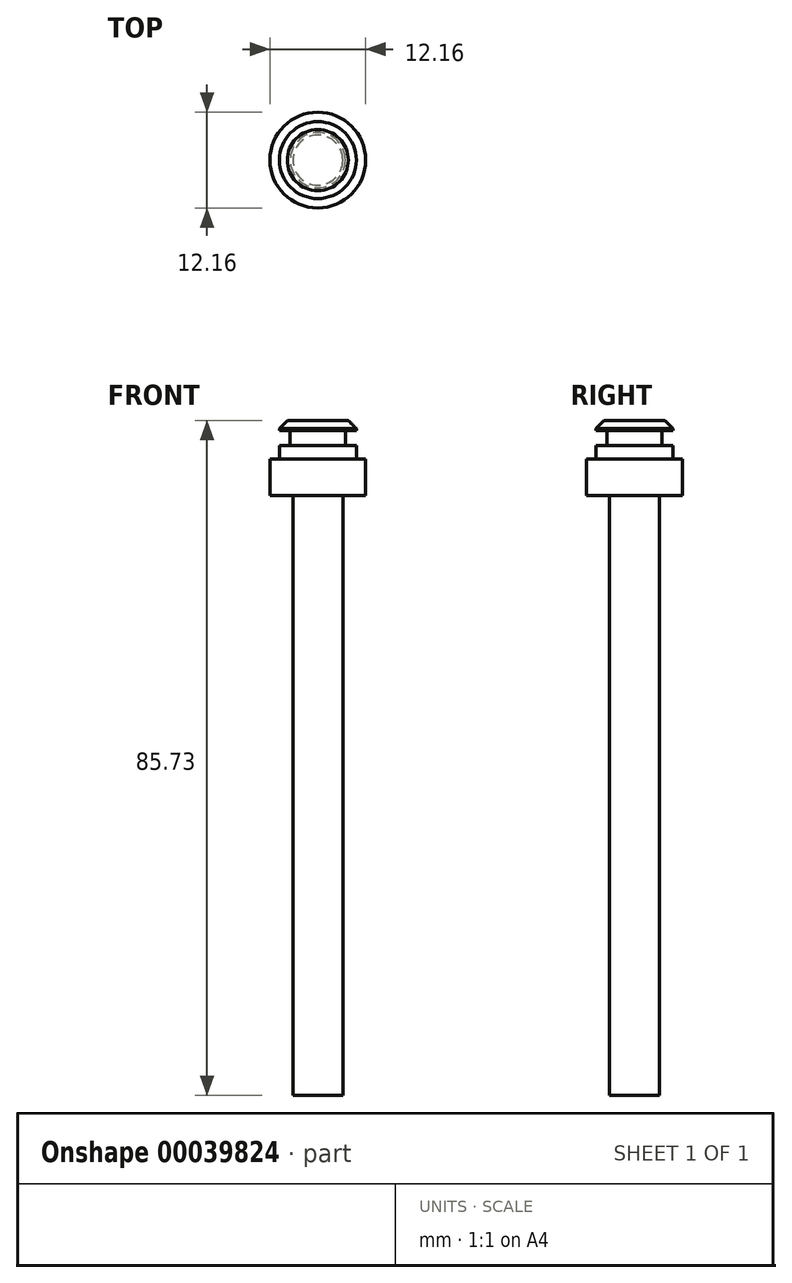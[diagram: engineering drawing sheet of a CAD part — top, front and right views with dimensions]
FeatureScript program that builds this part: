
annotation { "Feature Type Name" : "Feature", "Feature Type Description" : "" }
export const myFeature = defineFeature(function(context is Context, id is Id, definition is map)
    precondition{}
    {
        {
            var Q0;
            Q0=qCreatedBy(makeId("Top.planeOp"),FACE);
            var sketch = newSketch(context, id + "F0", { "sketchPlane" : qUnion([Q0])});
            skCircle(sketch, "E0", {"center": v(0, 0) * mm, "radius": 3.18 * mm});
            skSolve(sketch);
        }
        {
            var Q0;
            Q0 = qSketchRegion(id + "F0", true);
            extrude(context, id + "F1", {"entities" : qUnion([Q0]), "depth" : 76.2 * mm});
        }
        {
            var Q0;
            Q0=makeQuery(id+"F1.opExtrude","CAP_FACE",FACE,{"disambiguationData":[OSD([sQuery(id+"F0.wireOp",EDGE,"E0")])],"isStart":false});
            var sketch = newSketch(context, id + "F2", { "sketchPlane" : qUnion([Q0])});
            skCircle(sketch, "E1", {"center": v(0, 0) * mm, "radius": 6.08 * mm});
            skSolve(sketch);
        }
        {
            var Q0;
            Q0 = qSketchRegion(id + "F2", true);
            extrude(context, id + "F3", {"entities" : qUnion([Q0]), "operationType" : NewBodyOperationType.ADD, "depth" : 4.65 * mm});
        }
        {
            var Q0;
            Q0=makeQuery(id+"F3.opExtrude","CAP_FACE",FACE,{"disambiguationData":[OSD([sQuery(id+"F2.wireOp",EDGE,"E1")])],"isStart":false});
            var sketch = newSketch(context, id + "F4", { "sketchPlane" : qUnion([Q0])});
            skCircle(sketch, "E2", {"center": v(0, 0) * mm, "radius": 4.89 * mm});
            skSolve(sketch);
        }
        {
            var Q0;
            Q0 = qSketchRegion(id + "F4", true);
            extrude(context, id + "F5", {"entities" : qUnion([Q0]), "operationType" : NewBodyOperationType.ADD, "depth" : 4.88 * mm});
        }
        {
            var Q0;
            Q0=qCreatedBy(makeId("Front.planeOp"),FACE);
            var sketch = newSketch(context, id + "F6", { "sketchPlane" : qUnion([Q0])});
            skLineSegment(sketch, "E3", {"start": v(0, 88.66) * mm, "end": v(0, 38.2) * mm, "construction": true});
            skLineSegment(sketch, "E4.bottom", {"start": v(4.89, 84.43) * mm, "end": v(3.5, 84.43) * mm});
            skLineSegment(sketch, "E4.top", {"start": v(4.89, 82.52) * mm, "end": v(3.5, 82.52) * mm});
            skLineSegment(sketch, "E4.left", {"start": v(4.89, 84.43) * mm, "end": v(4.89, 82.52) * mm});
            skLineSegment(sketch, "E4.right", {"start": v(3.5, 84.43) * mm, "end": v(3.5, 82.52) * mm});
            skSolve(sketch);
        }
        {
            var Q0;
            Q0 = qSketchRegion(id + "F6", true);
            var Q1;
            Q1=sQuery(id+"F6.wireOp",EDGE,"E3");
            revolve(context, id + "F7", {"operationType" : NewBodyOperationType.REMOVE, "entities" : qUnion([Q0]), "axis" : qUnion([Q1]), "revolveType" : RevolveType.FULL, "oppositeDirection" : true});
        }
        {
            var Q0;
            Q0=makeQuery(id+"F5.opExtrude","CAP_EDGE",EDGE,{"disambiguationData":[OSD([sQuery(id+"F4.wireOp",EDGE,"E2")])],"isStart":false});
            chamfer(context, id + "F8", {"entities" : qUnion([Q0]), "width" : 1.02 * mm, "tangentPropagation" : true});
        }
    });
